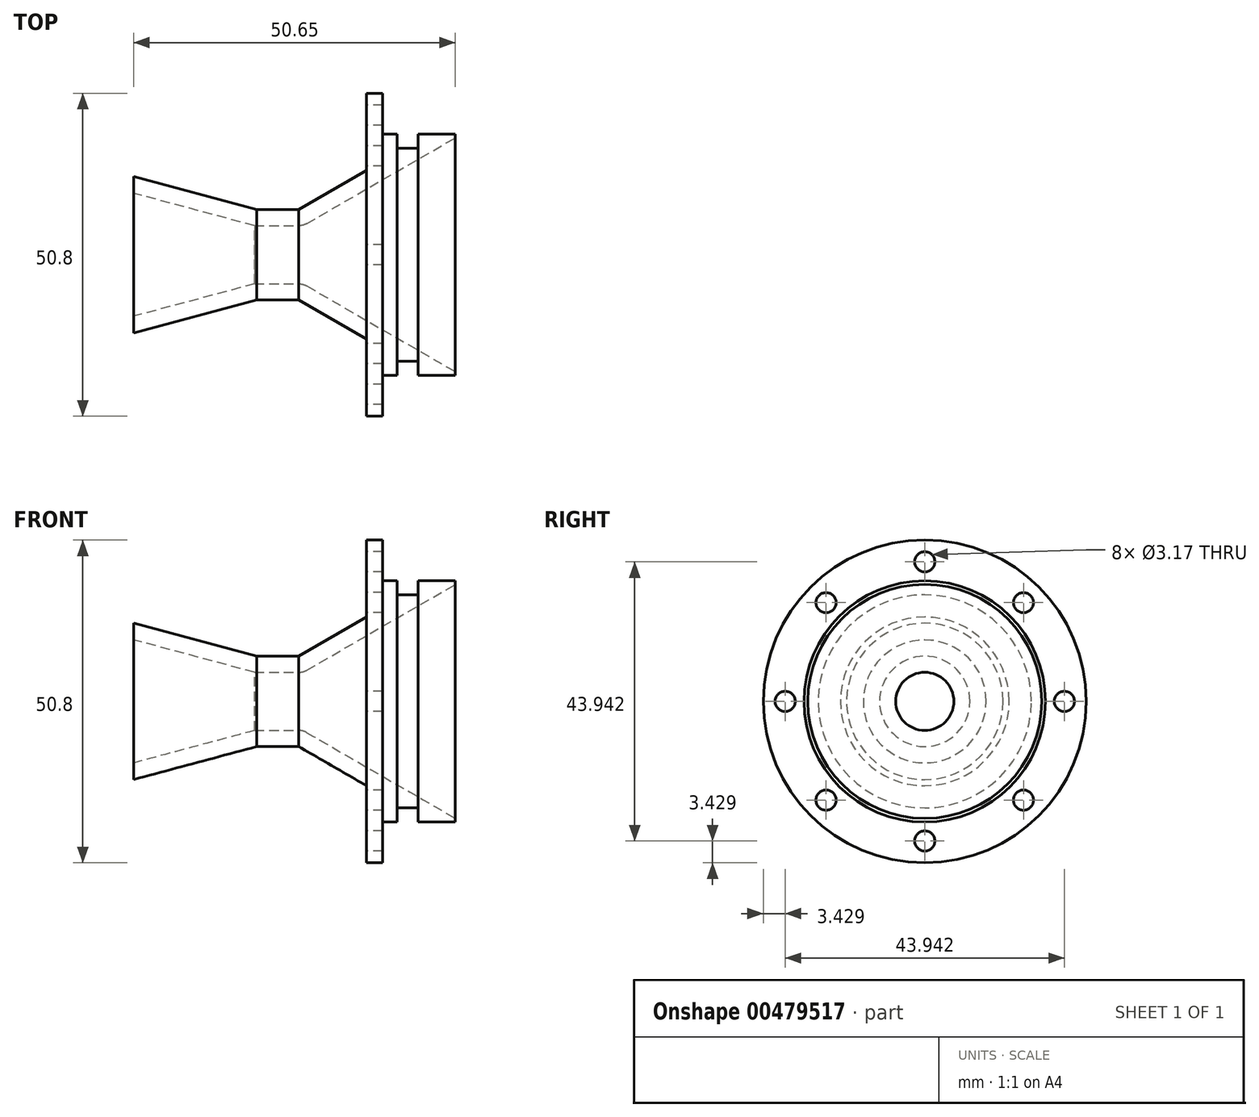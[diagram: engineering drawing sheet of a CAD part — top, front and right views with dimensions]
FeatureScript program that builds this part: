
annotation { "Feature Type Name" : "Feature", "Feature Type Description" : "" }
export const myFeature = defineFeature(function(context is Context, id is Id, definition is map)
    precondition{}
    {
        {
            var Q0;
            Q0=qCreatedBy(makeId("Front.planeOp"),FACE);
            var sketch = newSketch(context, id + "F0", { "sketchPlane" : qUnion([Q0])});
            skLineSegment(sketch, "E0", {"start": v(0, 0) * mm, "end": v(-35.88, 0) * mm, "construction": true});
            skLineSegment(sketch, "E1", {"start": v(0, 18.42) * mm, "end": v(0, 25.4) * mm});
            skLineSegment(sketch, "E2", {"start": v(0, 25.4) * mm, "end": v(-13.97, 25.4) * mm});
            skLineSegment(sketch, "E3", {"start": v(-13.97, 25.4) * mm, "end": v(-13.97, 13.28) * mm});
            skLineSegment(sketch, "E4", {"start": v(-13.97, 13.28) * mm, "end": v(-24.66, 7.11) * mm});
            skLineSegment(sketch, "E5", {"start": v(-24.66, 7.11) * mm, "end": v(-31.26, 7.11) * mm});
            skLineSegment(sketch, "E6", {"start": v(-31.26, 7.11) * mm, "end": v(-50.65, 12.3) * mm});
            skLineSegment(sketch, "E7", {"start": v(-50.65, 12.3) * mm, "end": v(-50.65, 9.68) * mm});
            skLineSegment(sketch, "E8", {"start": v(-50.65, 9.68) * mm, "end": v(-31.6, 4.57) * mm});
            skLineSegment(sketch, "E9", {"start": v(-31.6, 4.57) * mm, "end": v(-23.98, 4.57) * mm});
            skLineSegment(sketch, "E10", {"start": v(-23.98, 4.57) * mm, "end": v(0, 18.42) * mm});
            skSolve(sketch);
        }
        {
            var Q0;
            Q0 = qSketchRegion(id + "F0", true);
            var Q1;
            Q1=sQuery(id+"F0.wireOp",EDGE,"E0");
            revolve(context, id + "F1", {"entities" : qUnion([Q0]), "axis" : qUnion([Q1]), "revolveType" : RevolveType.FULL});
        }
        {
            var Q0;
            Q0=makeQuery(id+"F1.opRevolve","SWEPT_EDGE",EDGE,{"disambiguationData":[OSD([sQuery(id+"F0.wireOp",EDGE,"E9"),sQuery(id+"F0.wireOp",EDGE,"E10")])]});
            fillet(context, id + "F2", {"entities" : qUnion([Q0]), "radius" : 2.54 * mm, "tangentPropagation" : true, "allowEdgeOverflow" : false});
        }
        {
            var Q0;
            Q0=qCreatedBy(makeId("Front.planeOp"),FACE);
            var sketch = newSketch(context, id + "F3", { "sketchPlane" : qUnion([Q0])});
            skLineSegment(sketch, "E11", {"start": v(0, 0) * mm, "end": v(13.98, 0) * mm, "construction": true});
            skLineSegment(sketch, "E12", {"start": v(10.71, 18.99) * mm, "end": v(-11.43, 18.99) * mm});
            skLineSegment(sketch, "E13", {"start": v(-11.43, 18.99) * mm, "end": v(-11.43, 27.5) * mm});
            skLineSegment(sketch, "E14", {"start": v(-11.43, 27.5) * mm, "end": v(9.03, 27.5) * mm});
            skLineSegment(sketch, "E15", {"start": v(9.03, 27.5) * mm, "end": v(10.71, 18.99) * mm});
            skSolve(sketch);
        }
        {
            var Q0;
            Q0 = qSketchRegion(id + "F3", true);
            var Q1;
            Q1=sQuery(id+"F3.wireOp",EDGE,"E11");
            revolve(context, id + "F4", {"operationType" : NewBodyOperationType.REMOVE, "entities" : qUnion([Q0]), "axis" : qUnion([Q1]), "revolveType" : RevolveType.FULL, "oppositeDirection" : true});
        }
        {
            var Q0;
            Q0=qCreatedBy(makeId("Front.planeOp"),FACE);
            var sketch = newSketch(context, id + "F5", { "sketchPlane" : qUnion([Q0])});
            skLineSegment(sketch, "E16.bottom", {"start": v(-9.14, 21.72) * mm, "end": v(-5.84, 21.72) * mm});
            skLineSegment(sketch, "E16.top", {"start": v(-9.14, 16.76) * mm, "end": v(-5.84, 16.76) * mm});
            skLineSegment(sketch, "E16.left", {"start": v(-9.14, 21.72) * mm, "end": v(-9.14, 16.76) * mm});
            skLineSegment(sketch, "E16.right", {"start": v(-5.84, 21.72) * mm, "end": v(-5.84, 16.76) * mm});
            skLineSegment(sketch, "E17", {"start": v(0, 0) * mm, "end": v(9.07, 0) * mm, "construction": true});
            skSolve(sketch);
        }
        {
            var Q0;
            Q0 = qSketchRegion(id + "F5", true);
            var Q1;
            Q1=makeQuery(id+"F1.opRevolve","SWEPT_FACE",FACE,{"disambiguationData":[OSD([sQuery(id+"F0.wireOp",EDGE,"E5")])]});
            revolve(context, id + "F6", {"operationType" : NewBodyOperationType.REMOVE, "entities" : qUnion([Q0]), "axis" : qUnion([Q1]), "revolveType" : RevolveType.FULL, "oppositeDirection" : true});
        }
        {
            var Q0;
            Q0=makeQuery(id+"F1.opRevolve","SWEPT_FACE",FACE,{"disambiguationData":[OSD([sQuery(id+"F0.wireOp",EDGE,"E3")])]});
            var sketch = newSketch(context, id + "F7", { "sketchPlane" : qUnion([Q0])});
            skCircle(sketch, "E18", {"center": v(0, 0) * mm, "radius": 21.97 * mm, "construction": true});
            skPoint(sketch, "E19", {"position": v(0, 21.97) * mm});
            skLineSegment(sketch, "E20.anchor1", {"start": v(0, 0) * mm, "end": v(0, 21.97) * mm, "construction": true});
            skLineSegment(sketch, "E20.anchor2", {"start": v(0, 0) * mm, "end": v(0, 21.97) * mm, "construction": true});
            skPoint(sketch, "E21", {"position": v(15.54, 15.54) * mm});
            skPoint(sketch, "E22", {"position": v(21.97, 0) * mm});
            skPoint(sketch, "E23", {"position": v(0, -21.97) * mm});
            skPoint(sketch, "E24", {"position": v(15.54, -15.54) * mm});
            skPoint(sketch, "E25", {"position": v(-15.54, -15.54) * mm});
            skPoint(sketch, "E26", {"position": v(-21.97, 0) * mm});
            skPoint(sketch, "E27", {"position": v(-15.54, 15.54) * mm});
            skLineSegment(sketch, "E28", {"start": v(0, 0) * mm, "end": v(15.54, 15.54) * mm, "construction": true});
            skLineSegment(sketch, "E29", {"start": v(0, 0) * mm, "end": v(-10.87, 10.87) * mm});
            skSolve(sketch);
        }
        {
            var Q0;
            Q0=sQuery(id+"F7.wireOp",VERTEX,"E19");
            var Q1;
            Q1=sQuery(id+"F7.wireOp",VERTEX,"E21");
            var Q2;
            Q2=sQuery(id+"F7.wireOp",VERTEX,"E22");
            var Q3;
            Q3=sQuery(id+"F7.wireOp",VERTEX,"E24");
            var Q4;
            Q4=sQuery(id+"F7.wireOp",VERTEX,"E23");
            var Q5;
            Q5=sQuery(id+"F7.wireOp",VERTEX,"E25");
            var Q6;
            Q6=sQuery(id+"F7.wireOp",VERTEX,"E26");
            var Q7;
            Q7=sQuery(id+"F7.wireOp",VERTEX,"E27");
            var Q8;
            Q8=makeQuery(id+"F1.opRevolve","SWEPT_BODY",BODY,{"disambiguationData":[OSD([sQuery(id+"F0.wireOp",EDGE,"E1"),sQuery(id+"F0.wireOp",EDGE,"E2"),sQuery(id+"F0.wireOp",EDGE,"E3"),sQuery(id+"F0.wireOp",EDGE,"E4"),sQuery(id+"F0.wireOp",EDGE,"E5"),sQuery(id+"F0.wireOp",EDGE,"E6"),sQuery(id+"F0.wireOp",EDGE,"E7"),sQuery(id+"F0.wireOp",EDGE,"E8"),sQuery(id+"F0.wireOp",EDGE,"E9"),sQuery(id+"F0.wireOp",EDGE,"E10")])]});
            hole(context, id + "F8", {"style" : HoleStyle.SIMPLE, "endStyle" : HoleEndStyle.THROUGH, "holeDiameter" : 3.17 * mm, "isTappedThrough" : true, "tappedDepth" : 12.7 * mm, "tapClearance" : 3, "locations" : qUnion([Q0, Q1, Q2, Q3, Q4, Q5, Q6, Q7]), "scope" : qUnion([Q8])});
        }
    });
